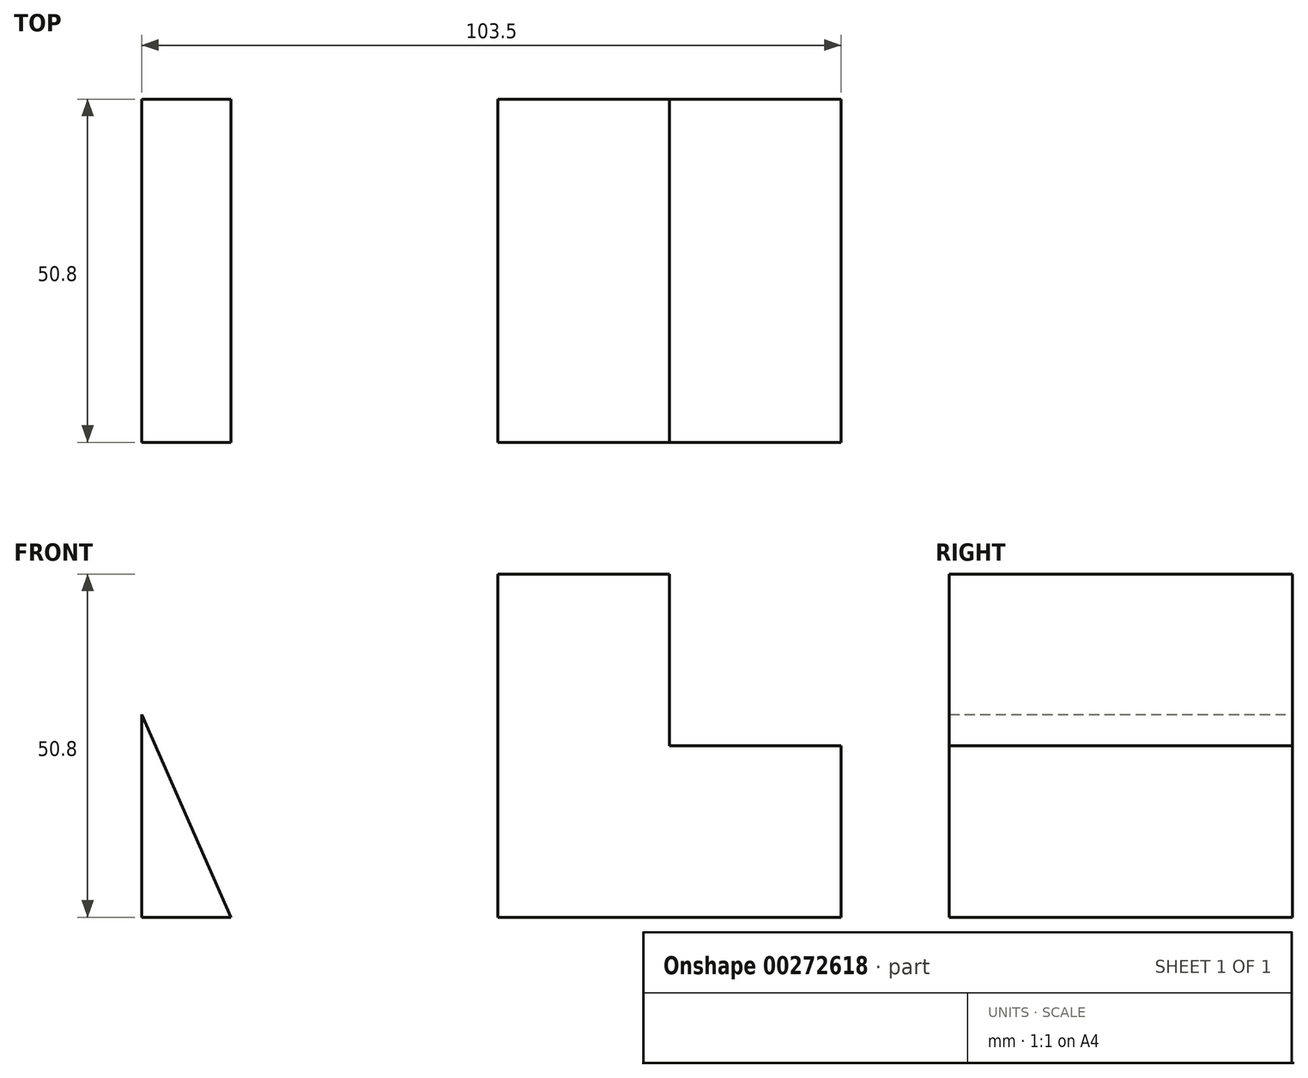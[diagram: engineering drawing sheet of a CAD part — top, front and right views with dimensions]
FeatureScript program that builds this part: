
annotation { "Feature Type Name" : "Feature", "Feature Type Description" : "" }
export const myFeature = defineFeature(function(context is Context, id is Id, definition is map)
    precondition{}
    {
        {
            var Q0;
            Q0=qCreatedBy(makeId("Front.planeOp"),FACE);
            var sketch = newSketch(context, id + "F0", { "sketchPlane" : qUnion([Q0])});
            skLineSegment(sketch, "E0", {"start": v(0, 0) * mm, "end": v(-52.7, 0) * mm});
            skLineSegment(sketch, "E1", {"start": v(0, 0) * mm, "end": v(-9.55, 2.86) * mm});
            skLineSegment(sketch, "E2", {"start": v(-52.7, 0) * mm, "end": v(-52.7, 42.2) * mm});
            skLineSegment(sketch, "E3", {"start": v(-52.7, 29.98) * mm, "end": v(-32.2, -16.5) * mm});
            skLineSegment(sketch, "E4", {"start": v(-32.2, -16.5) * mm, "end": v(-3.82, -5.54) * mm});
            skLineSegment(sketch, "E5", {"start": v(0, 0) * mm, "end": v(50.8, 0) * mm});
            skLineSegment(sketch, "E6", {"start": v(50.8, 0) * mm, "end": v(50.8, 25.4) * mm});
            skLineSegment(sketch, "E7", {"start": v(50.8, 25.4) * mm, "end": v(25.4, 25.4) * mm});
            skLineSegment(sketch, "E8", {"start": v(0, 0) * mm, "end": v(0, 50.8) * mm});
            skLineSegment(sketch, "E9", {"start": v(0, 50.8) * mm, "end": v(25.4, 50.8) * mm});
            skLineSegment(sketch, "E10", {"start": v(25.4, 50.8) * mm, "end": v(25.4, 25.4) * mm});
            skSolve(sketch);
        }
        {
            var Q0;
            Q0 = qSketchRegion(id + "F0", true);
            extrude(context, id + "F1", {"entities" : qUnion([Q0]), "depth" : 50.8 * mm});
        }
    });
